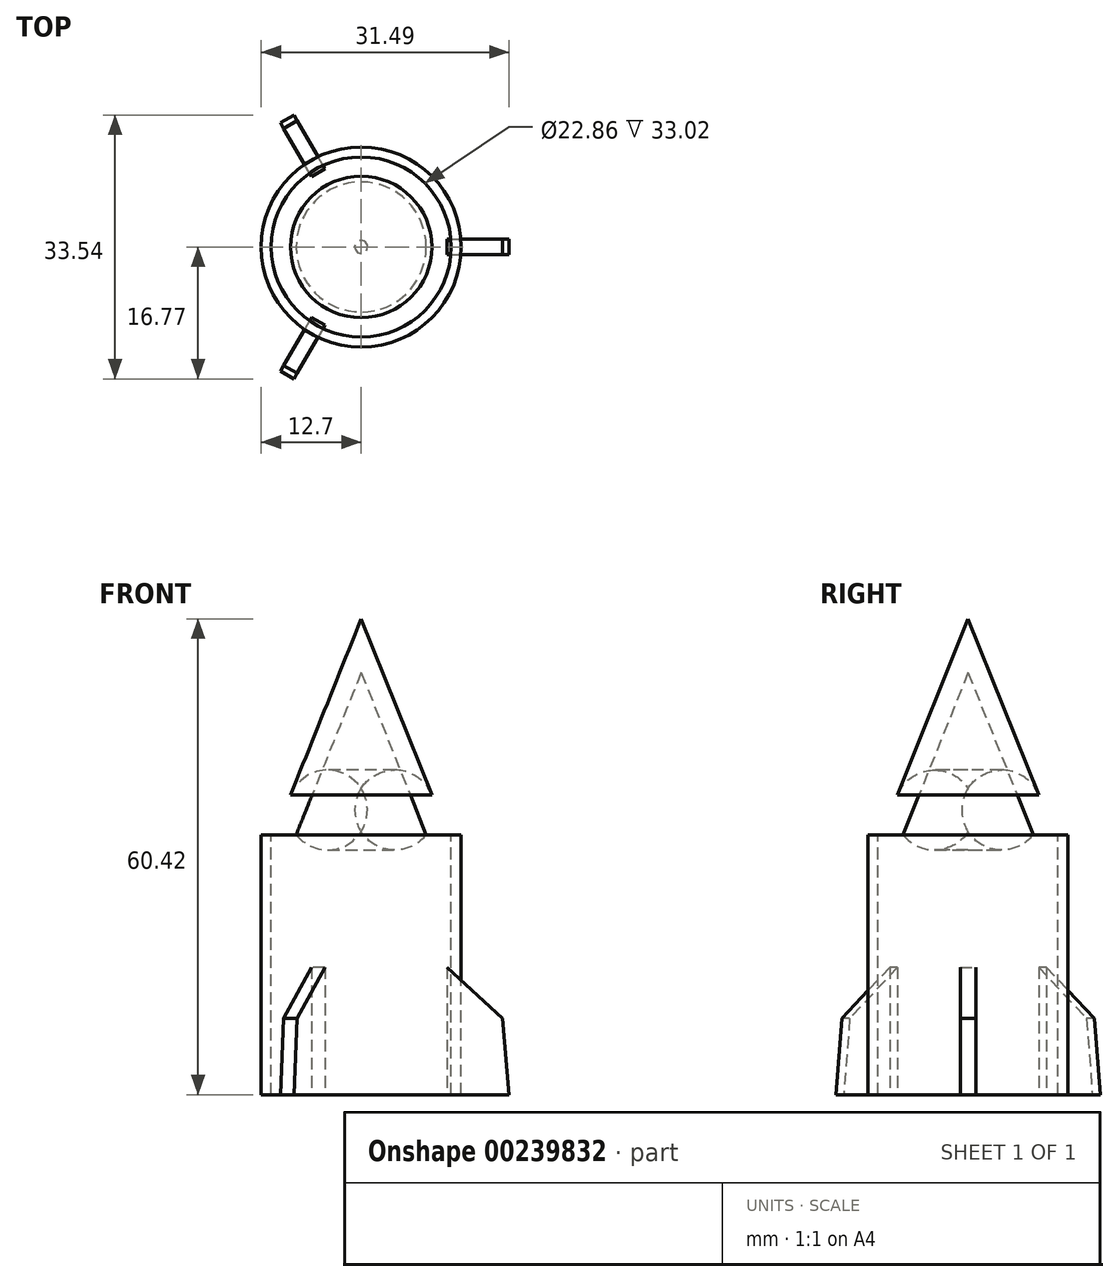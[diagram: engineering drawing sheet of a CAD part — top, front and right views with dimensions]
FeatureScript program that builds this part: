
annotation { "Feature Type Name" : "Feature", "Feature Type Description" : "" }
export const myFeature = defineFeature(function(context is Context, id is Id, definition is map)
    precondition{}
    {
        {
            var Q0;
            Q0=qCreatedBy(makeId("Top.planeOp"),FACE);
            var sketch = newSketch(context, id + "F0", { "sketchPlane" : qUnion([Q0])});
            skCircle(sketch, "E0", {"center": v(0, 0) * mm, "radius": 12.7 * mm});
            skCircle(sketch, "E1", {"center": v(0, 0) * mm, "radius": 11.43 * mm});
            skSolve(sketch);
        }
        {
            var Q0;
            Q0=makeQuery(id+"F0.imprint","IMPRINT",FACE,{"disambiguationData":[TD([[makeQuery(id+"F0.imprint","IMPRINT",EDGE,{"derivedFrom":sQuery(id+"F0.wireOp",EDGE,"E0")}),1.0]])]});
            extrude(context, id + "F1", {"entities" : qUnion([Q0]), "oppositeDirection" : true, "depth" : 33.02 * mm});
        }
        {
            var Q0;
            Q0=qCreatedBy(makeId("Front.planeOp"),FACE);
            var sketch = newSketch(context, id + "F2", { "sketchPlane" : qUnion([Q0])});
            skLineSegment(sketch, "E2", {"start": v(-11, 0) * mm, "end": v(0, 27.4) * mm});
            skLineSegment(sketch, "E3", {"start": v(-11, 0) * mm, "end": v(0, 0) * mm});
            skLineSegment(sketch, "E4", {"start": v(0, 27.4) * mm, "end": v(0, 0) * mm});
            skSolve(sketch);
        }
        {
            var Q0;
            Q0 = qSketchRegion(id + "F2", true);
            var Q1;
            Q1=sQuery(id+"F2.wireOp",EDGE,"E4");
            revolve(context, id + "F3", {"operationType" : NewBodyOperationType.ADD, "entities" : qUnion([Q0]), "axis" : qUnion([Q1]), "revolveType" : RevolveType.FULL});
        }
        {
            var Q0;
            Q0=makeQuery(id+"F3.opRevolve","SWEPT_FACE",FACE,{"disambiguationData":[OSD([sQuery(id+"F2.wireOp",EDGE,"E3")])]});
            shell(context, id + "F4", {"entities" : qUnion([Q0]), "thickness" : 2.54 * mm});
        }
        {
            var Q0;
            Q0=makeQuery(id+"F3.opRevolve","SWEPT_FACE",FACE,{"disambiguationData":[OSD([sQuery(id+"F2.wireOp",EDGE,"E2")])]});
            fillet(context, id + "F5", {"entities" : qUnion([Q0]), "radius" : 5.08 * mm, "tangentPropagation" : true, "allowEdgeOverflow" : false});
        }
        {
            var Q0;
            Q0=qCreatedBy(makeId("Front.planeOp"),FACE);
            var sketch = newSketch(context, id + "F6", { "sketchPlane" : qUnion([Q0])});
            skLineSegment(sketch, "E5", {"start": v(10.92, -16.84) * mm, "end": v(17.95, -23.34) * mm});
            skLineSegment(sketch, "E6", {"start": v(10.92, -33.02) * mm, "end": v(18.8, -33.02) * mm});
            skLineSegment(sketch, "E7", {"start": v(17.95, -23.34) * mm, "end": v(18.8, -33.02) * mm});
            skLineSegment(sketch, "E8", {"start": v(10.92, -16.84) * mm, "end": v(10.92, -33.02) * mm});
            skSolve(sketch);
        }
        {
            var Q0;
            Q0 = qSketchRegion(id + "F6", true);
            extrude(context, id + "F7", {"entities" : qUnion([Q0]), "endBound" : BoundingType.SYMMETRIC, "depth" : 1.98 * mm});
        }
        {
            var Q0;
            Q0=makeQuery(id+"F7.opExtrude","SWEPT_BODY",BODY,{"disambiguationData":[OSD([sQuery(id+"F6.wireOp",EDGE,"E5"),sQuery(id+"F6.wireOp",EDGE,"E6"),sQuery(id+"F6.wireOp",EDGE,"E7"),sQuery(id+"F6.wireOp",EDGE,"StI7iNDn-EBAO-2glr-oy2C-w2Kcs1DJi5YX")])]});
            var Q1;
            Q1=makeQuery(id+"F1.opExtrude","CAP_EDGE",EDGE,{"disambiguationData":[OSD([sQuery(id+"F0.wireOp",EDGE,"E0")])],"isStart":false});
            circularPattern(context, id + "F8", {"entities" : qUnion([Q0]), "axis" : qUnion([Q1]), "angle" : 360 * degree, "instanceCount" : 3, "equalSpace" : true});
        }
    });
